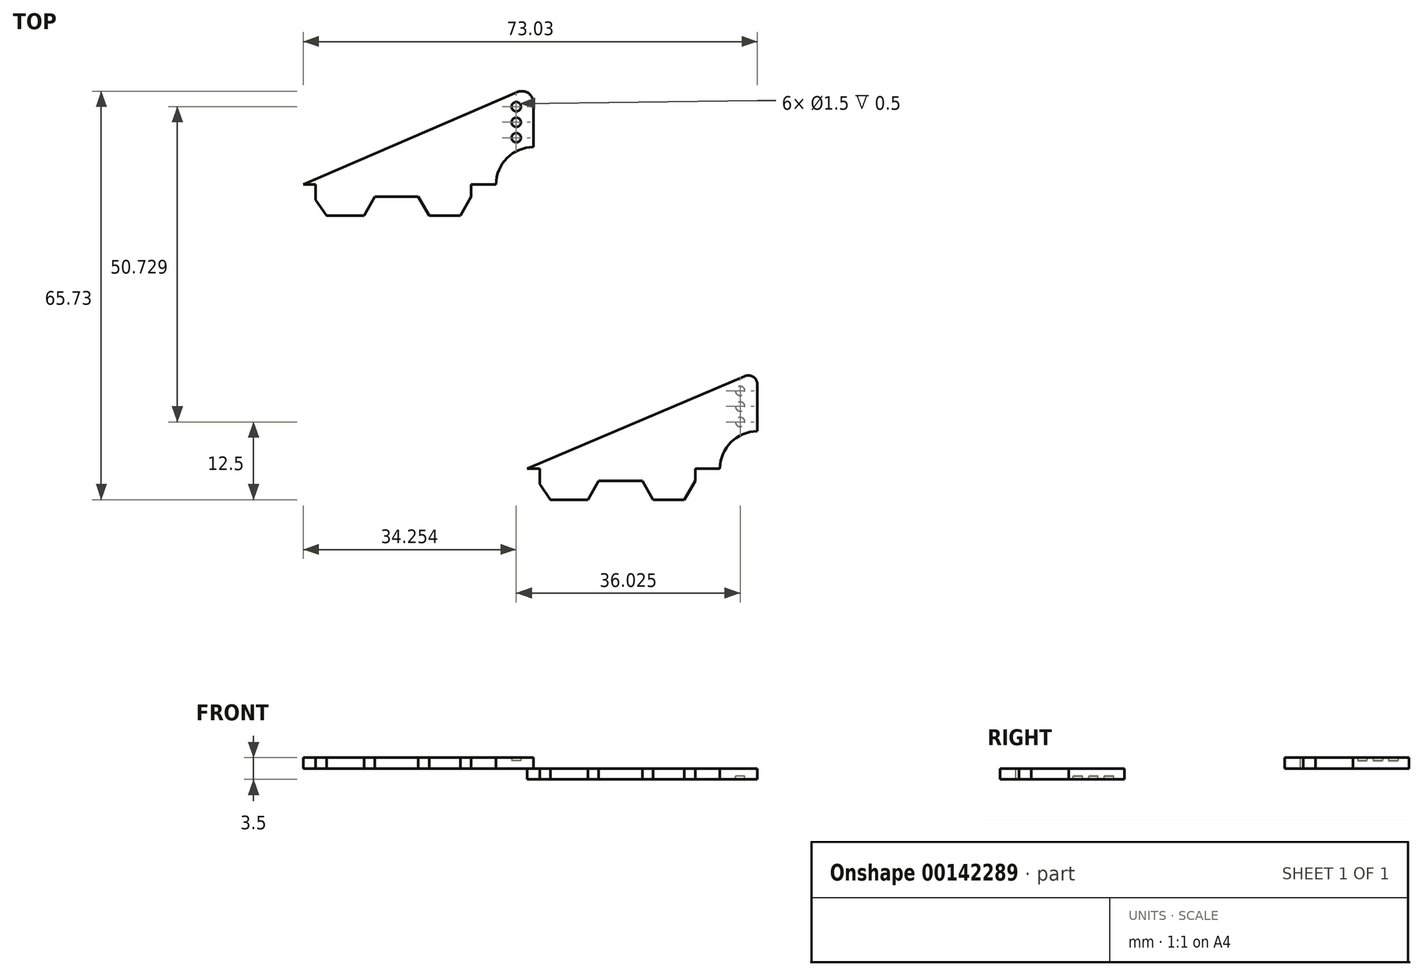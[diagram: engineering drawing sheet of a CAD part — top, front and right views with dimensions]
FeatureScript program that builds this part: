
annotation { "Feature Type Name" : "Feature", "Feature Type Description" : "" }
export const myFeature = defineFeature(function(context is Context, id is Id, definition is map)
    precondition{}
    {
        {
            var Q0;
            Q0=qCreatedBy(makeId("Top.planeOp"),FACE);
            var sketch = newSketch(context, id + "F0", { "sketchPlane" : qUnion([Q0])});
            skLineSegment(sketch, "E0.bottom", {"start": v(-58.02, 61.7) * mm, "end": v(-21.02, 61.7) * mm});
            skLineSegment(sketch, "E0.top", {"start": v(-58.02, 40.73) * mm, "end": v(-21.02, 40.73) * mm});
            skLineSegment(sketch, "E0.left", {"start": v(-58.02, 61.7) * mm, "end": v(-58.02, 40.73) * mm});
            skLineSegment(sketch, "E0.right", {"start": v(-21.02, 61.7) * mm, "end": v(-21.02, 40.73) * mm});
            skLineSegment(sketch, "E1.bottom", {"start": v(-21.02, 40.73) * mm, "end": v(-31.02, 40.73) * mm});
            skLineSegment(sketch, "E1.top", {"start": v(-21.02, 45.73) * mm, "end": v(-31.02, 45.73) * mm});
            skLineSegment(sketch, "E1.left", {"start": v(-21.02, 40.73) * mm, "end": v(-21.02, 45.73) * mm});
            skLineSegment(sketch, "E1.right", {"start": v(-31.02, 40.73) * mm, "end": v(-31.02, 45.73) * mm});
            skLineSegment(sketch, "E2", {"start": v(-58.02, 45.73) * mm, "end": v(-21.02, 61.7) * mm});
            skLineSegment(sketch, "E3", {"start": v(-56.02, 45.73) * mm, "end": v(-56.02, 40.73) * mm});
            skLineSegment(sketch, "E4", {"start": v(-58.02, 45.73) * mm, "end": v(-56.02, 45.73) * mm});
            skLineSegment(sketch, "E5.bottom", {"start": v(-46.52, 40.73) * mm, "end": v(-39.52, 40.73) * mm});
            skLineSegment(sketch, "E5.top", {"start": v(-46.52, 43.73) * mm, "end": v(-39.52, 43.73) * mm});
            skLineSegment(sketch, "E5.left", {"start": v(-46.52, 40.73) * mm, "end": v(-46.52, 43.73) * mm});
            skLineSegment(sketch, "E5.right", {"start": v(-39.52, 40.73) * mm, "end": v(-39.52, 43.73) * mm});
            skLineSegment(sketch, "E6", {"start": v(-46.52, 43.73) * mm, "end": v(-48.27, 40.73) * mm});
            skLineSegment(sketch, "E7", {"start": v(-56.02, 43.23) * mm, "end": v(-54.27, 40.73) * mm});
            skLineSegment(sketch, "E8", {"start": v(-39.52, 43.73) * mm, "end": v(-37.77, 40.73) * mm});
            skLineSegment(sketch, "E9", {"start": v(-31.02, 43.73) * mm, "end": v(-32.77, 40.73) * mm});
            skArc(sketch, "E10", {"start": v(-21.02, 51.73) * mm, "mid": v(-25.26, 49.97) * mm, "end": v(-27.02, 45.73) * mm});
            skArc(sketch, "E11", {"start": v(-21.02, 58.88) * mm, "mid": v(-21.85, 60.42) * mm, "end": v(-23.6, 60.58) * mm});
            skLineSegment(sketch, "E12", {"start": v(-46.69, 60.73) * mm, "end": v(-21.02, 60.73) * mm, "construction": true});
            skCircle(sketch, "E13", {"center": v(-23.77, 58.23) * mm, "radius": 0.75 * mm});
            skCircle(sketch, "E14", {"center": v(-23.77, 55.73) * mm, "radius": 0.75 * mm});
            skCircle(sketch, "E15", {"center": v(-23.77, 53.23) * mm, "radius": 0.75 * mm});
            skLineSegment(sketch, "E16", {"start": v(-23.02, 65.6) * mm, "end": v(-23.02, 35.2) * mm, "construction": true});
            skSolve(sketch);
        }
        {
            var Q0;
            Q0=qCreatedBy(makeId("Top.planeOp"),FACE);
            var sketch = newSketch(context, id + "F1", { "sketchPlane" : qUnion([Q0])});
            skLineSegment(sketch, "E17.bottom", {"start": v(-22, 15.74) * mm, "end": v(15, 15.74) * mm});
            skLineSegment(sketch, "E17.top", {"start": v(-22, -5) * mm, "end": v(15, -5) * mm});
            skLineSegment(sketch, "E17.left", {"start": v(-22, 15.74) * mm, "end": v(-22, -5) * mm});
            skLineSegment(sketch, "E17.right", {"start": v(15, 15.74) * mm, "end": v(15, -5) * mm});
            skLineSegment(sketch, "E18.bottom", {"start": v(15, -5) * mm, "end": v(5, -5) * mm});
            skLineSegment(sketch, "E18.top", {"start": v(15, 0) * mm, "end": v(5, 0) * mm});
            skLineSegment(sketch, "E18.left", {"start": v(15, -5) * mm, "end": v(15, 0) * mm});
            skLineSegment(sketch, "E18.right", {"start": v(5, -5) * mm, "end": v(5, 0) * mm});
            skLineSegment(sketch, "E19", {"start": v(-22, 15.74) * mm, "end": v(-22, 0) * mm});
            skLineSegment(sketch, "E20", {"start": v(-22, 0) * mm, "end": v(-22, 15.74) * mm});
            skLineSegment(sketch, "E21", {"start": v(-22, 0) * mm, "end": v(15, 15.74) * mm});
            skLineSegment(sketch, "E22.bottom", {"start": v(-22, -5) * mm, "end": v(-20, -5) * mm});
            skLineSegment(sketch, "E22.top", {"start": v(-22, 0) * mm, "end": v(-20, 0) * mm});
            skLineSegment(sketch, "E22.left", {"start": v(-22, -5) * mm, "end": v(-22, 0) * mm});
            skLineSegment(sketch, "E22.right", {"start": v(-20, -5) * mm, "end": v(-20, 0) * mm});
            skLineSegment(sketch, "E23.bottom", {"start": v(-10.5, -5) * mm, "end": v(-3.5, -5) * mm});
            skLineSegment(sketch, "E23.top", {"start": v(-10.5, -2) * mm, "end": v(-3.5, -2) * mm});
            skLineSegment(sketch, "E23.left", {"start": v(-10.5, -5) * mm, "end": v(-10.5, -2) * mm});
            skLineSegment(sketch, "E23.right", {"start": v(-3.5, -5) * mm, "end": v(-3.5, -2) * mm});
            skLineSegment(sketch, "E24", {"start": v(-20, -5) * mm, "end": v(-10.5, -5) * mm});
            skLineSegment(sketch, "E25", {"start": v(-3.5, -5) * mm, "end": v(5, -5) * mm});
            skLineSegment(sketch, "E26", {"start": v(-20, -2.5) * mm, "end": v(-18.24, -5) * mm});
            skLineSegment(sketch, "E27", {"start": v(-20, -5) * mm, "end": v(-18.24, -5) * mm});
            skLineSegment(sketch, "E28", {"start": v(-10.5, -2) * mm, "end": v(-12.24, -5) * mm});
            skLineSegment(sketch, "E29", {"start": v(-12.24, -5) * mm, "end": v(-10.5, -5) * mm});
            skLineSegment(sketch, "E30", {"start": v(-3.5, -2) * mm, "end": v(-1.74, -5) * mm});
            skLineSegment(sketch, "E31", {"start": v(-3.5, -5) * mm, "end": v(-1.74, -5) * mm});
            skLineSegment(sketch, "E32", {"start": v(5, -2) * mm, "end": v(3.26, -5) * mm});
            skLineSegment(sketch, "E33", {"start": v(3.26, -5) * mm, "end": v(5, -5) * mm});
            skLineSegment(sketch, "E34", {"start": v(15, 15.74) * mm, "end": v(15, 6) * mm});
            skArc(sketch, "E35", {"start": v(15, 6) * mm, "mid": v(10.77, 4.24) * mm, "end": v(9, 0) * mm});
            skArc(sketch, "E36", {"start": v(15, 13.55) * mm, "mid": v(14.36, 14.76) * mm, "end": v(13, 14.88) * mm});
            skLineSegment(sketch, "E37", {"start": v(-10.9, 15) * mm, "end": v(6.65, 15) * mm, "construction": true});
            skLineSegment(sketch, "E38", {"start": v(6.65, 15) * mm, "end": v(38.36, 15) * mm, "construction": true});
            skCircle(sketch, "E39", {"center": v(12.26, 12.5) * mm, "radius": 0.75 * mm});
            skCircle(sketch, "E40", {"center": v(12.26, 10) * mm, "radius": 0.75 * mm});
            skCircle(sketch, "E41", {"center": v(12.26, 7.5) * mm, "radius": 0.75 * mm});
            skLineSegment(sketch, "E42", {"start": v(13, 29.85) * mm, "end": v(13, -23.82) * mm, "construction": true});
            skSolve(sketch);
        }
        {
            var Q0;
            {var subQ2=sQuery(id+"F1.wireOp",EDGE,"E22.top");Q0=makeQuery(id+"F1.imprint","IMPRINT",FACE,{"disambiguationData":[TD([[makeQuery(id+"F1.imprint","IMPRINT",EDGE,{"derivedFrom":subQ2}),1.0]])]});}
            extrude(context, id + "F2", {"entities" : qUnion([Q0]), "oppositeDirection" : true, "depth" : 1.75 * mm});
        }
        {
            var Q0;
            {var subQ0=sQuery(id+"F0.wireOp",EDGE,"E4");Q0=makeQuery(id+"F0.imprint","IMPRINT",FACE,{"disambiguationData":[TD([[makeQuery(id+"F0.imprint","IMPRINT",EDGE,{"derivedFrom":subQ0}),1.0]])]});}
            extrude(context, id + "F3", {"entities" : qUnion([Q0]), "depth" : 1.75 * mm});
        }
        {
            var Q0;
            Q0=makeQuery(id+"F1.imprint","IMPRINT",FACE,{"disambiguationData":[TD([[makeQuery(id+"F1.imprint","IMPRINT",EDGE,{"derivedFrom":sQuery(id+"F1.wireOp",EDGE,"E39")}),1.0]])]});
            var Q1;
            Q1=makeQuery(id+"F1.imprint","IMPRINT",FACE,{"disambiguationData":[TD([[makeQuery(id+"F1.imprint","IMPRINT",EDGE,{"derivedFrom":sQuery(id+"F1.wireOp",EDGE,"E40")}),1.0]])]});
            var Q2;
            Q2=makeQuery(id+"F1.imprint","IMPRINT",FACE,{"disambiguationData":[TD([[makeQuery(id+"F1.imprint","IMPRINT",EDGE,{"derivedFrom":sQuery(id+"F1.wireOp",EDGE,"E41")}),1.0]])]});
            extrude(context, id + "F4", {"entities" : qUnion([Q0, Q1, Q2]), "operationType" : NewBodyOperationType.ADD, "oppositeDirection" : true, "depth" : 1.25 * mm});
        }
        {
            var Q0;
            Q0=makeQuery(id+"F0.imprint","IMPRINT",FACE,{"disambiguationData":[TD([[makeQuery(id+"F0.imprint","IMPRINT",EDGE,{"derivedFrom":sQuery(id+"F0.wireOp",EDGE,"E13")}),1.0]])]});
            var Q1;
            Q1=makeQuery(id+"F0.imprint","IMPRINT",FACE,{"disambiguationData":[TD([[makeQuery(id+"F0.imprint","IMPRINT",EDGE,{"derivedFrom":sQuery(id+"F0.wireOp",EDGE,"E14")}),1.0]])]});
            var Q2;
            Q2=makeQuery(id+"F0.imprint","IMPRINT",FACE,{"disambiguationData":[TD([[makeQuery(id+"F0.imprint","IMPRINT",EDGE,{"derivedFrom":sQuery(id+"F0.wireOp",EDGE,"E15")}),1.0]])]});
            extrude(context, id + "F5", {"entities" : qUnion([Q0, Q1, Q2]), "operationType" : NewBodyOperationType.ADD, "depth" : 1.25 * mm});
        }
    });
